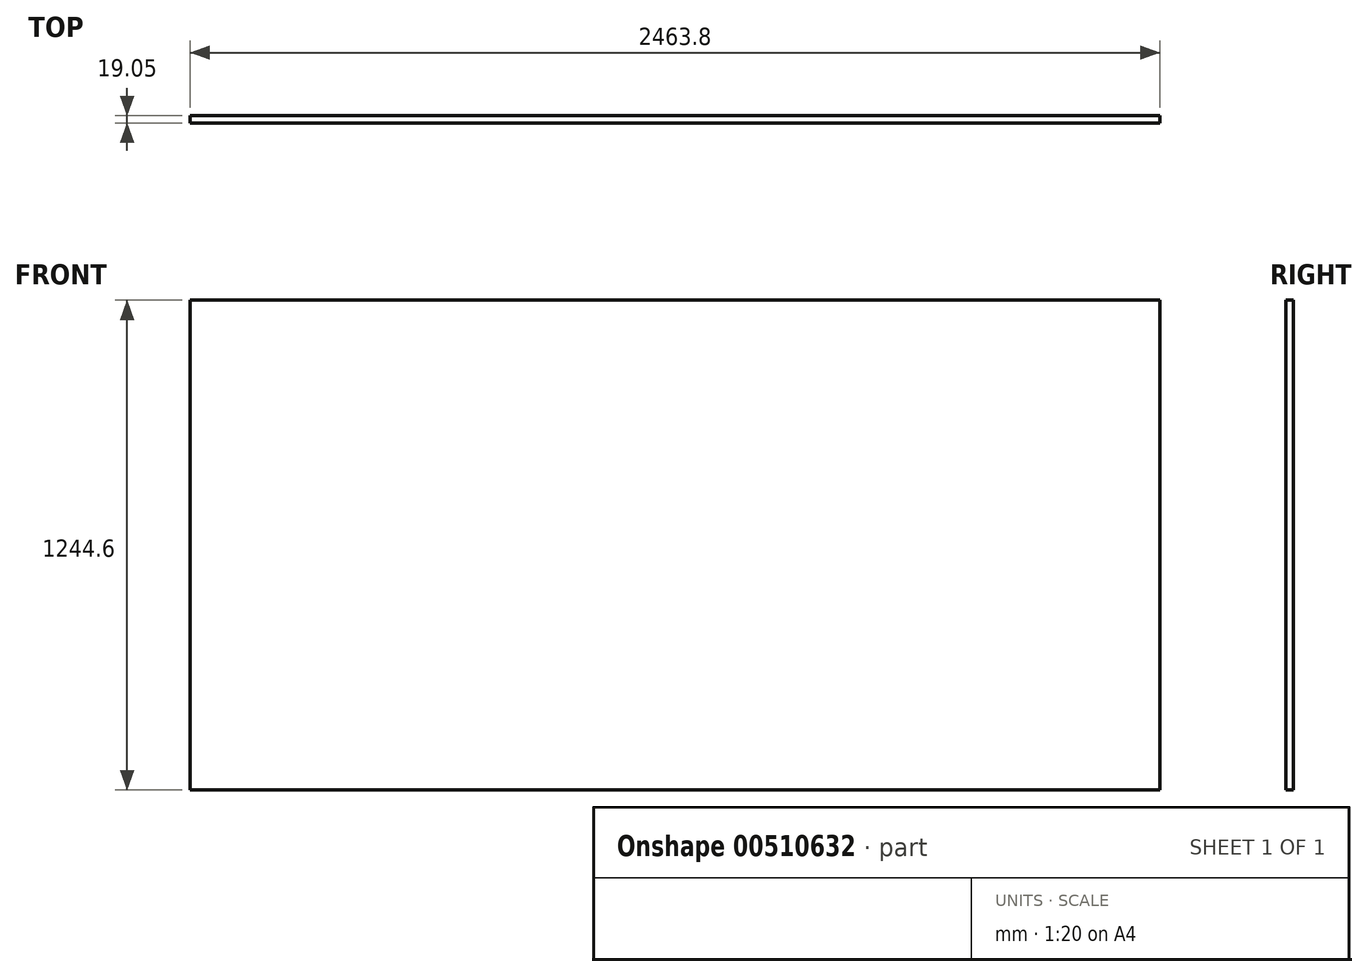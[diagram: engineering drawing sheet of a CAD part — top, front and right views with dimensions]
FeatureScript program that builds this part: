
annotation { "Feature Type Name" : "Feature", "Feature Type Description" : "" }
export const myFeature = defineFeature(function(context is Context, id is Id, definition is map)
    precondition{}
    {
        {
            var Q0;
            Q0=qCreatedBy(makeId("Front.planeOp"),FACE);
            var sketch = newSketch(context, id + "F0", { "sketchPlane" : qUnion([Q0])});
            skLineSegment(sketch, "E0", {"start": v(0, 622.3) * mm, "end": v(1231.9, 622.3) * mm});
            skLineSegment(sketch, "E1", {"start": v(1231.9, 622.3) * mm, "end": v(1231.9, 0) * mm});
            skLineSegment(sketch, "E2.MirrorCS", {"start": v(0, -622.3) * mm, "end": v(1231.9, -622.3) * mm});
            skLineSegment(sketch, "E3.MirrorCS", {"start": v(1231.9, -622.3) * mm, "end": v(1231.9, 0) * mm});
            skLineSegment(sketch, "E4.MirrorCS", {"start": v(-1231.9, -622.3) * mm, "end": v(-1231.9, 0) * mm});
            skLineSegment(sketch, "E5.MirrorCS", {"start": v(-1231.9, 622.3) * mm, "end": v(-1231.9, 0) * mm});
            skLineSegment(sketch, "E6.MirrorCS", {"start": v(0, -622.3) * mm, "end": v(-1231.9, -622.3) * mm});
            skLineSegment(sketch, "E7.MirrorCS", {"start": v(0, 622.3) * mm, "end": v(-1231.9, 622.3) * mm});
            skSolve(sketch);
        }
        {
            var Q0;
            Q0 = qSketchRegion(id + "F0", true);
            extrude(context, id + "F1", {"entities" : qUnion([Q0]), "depth" : 19.05 * mm});
        }
    });
